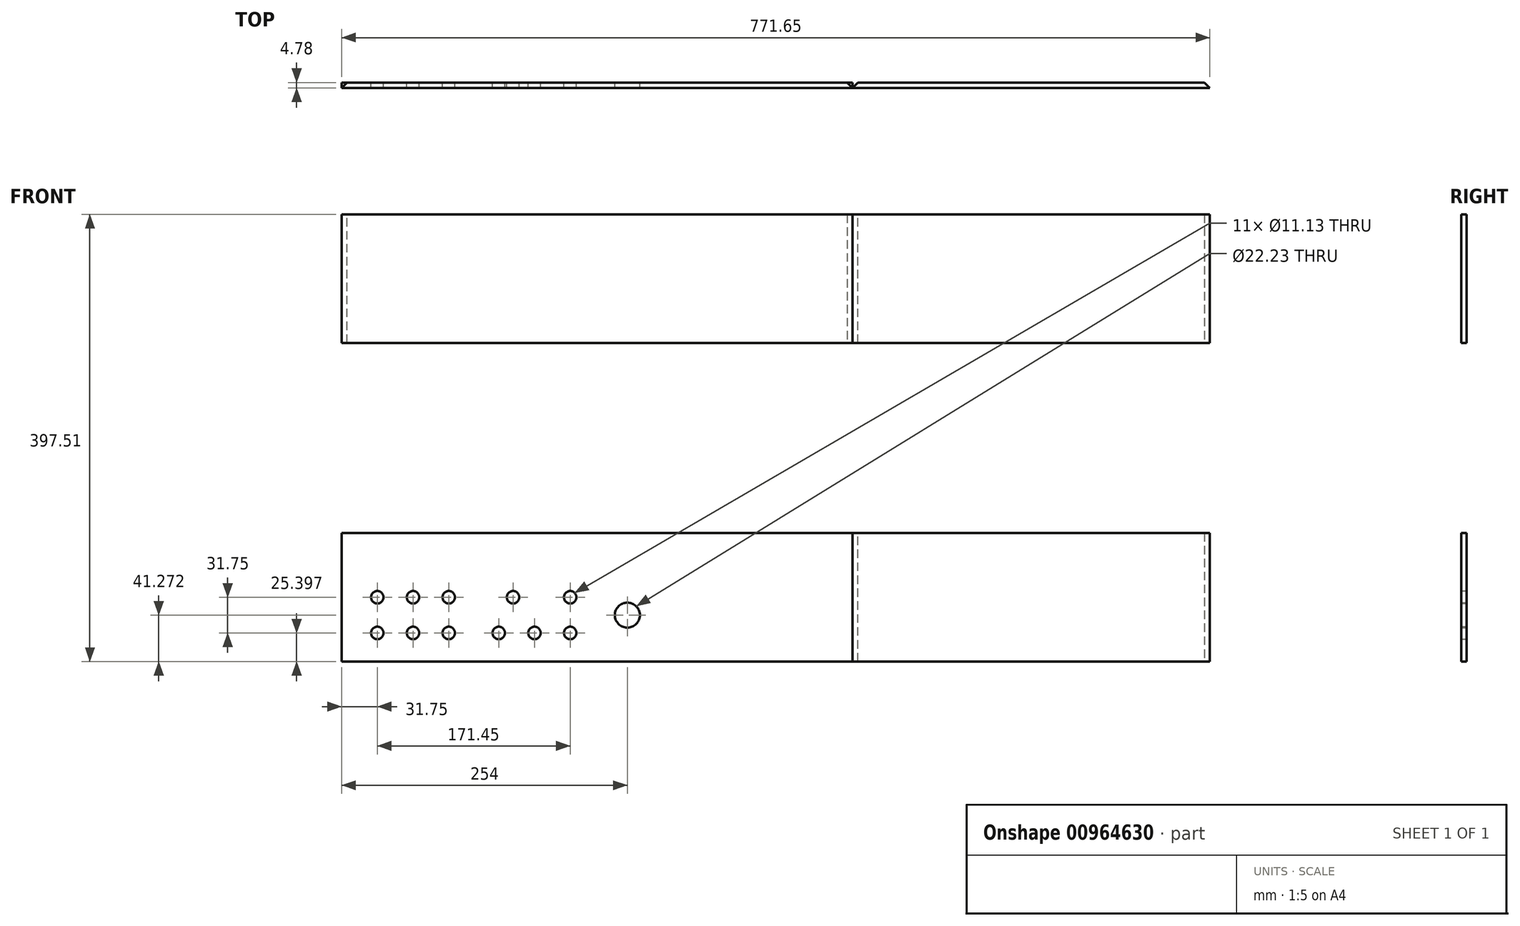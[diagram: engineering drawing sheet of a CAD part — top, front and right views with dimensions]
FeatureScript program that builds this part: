
annotation { "Feature Type Name" : "Feature", "Feature Type Description" : "" }
export const myFeature = defineFeature(function(context is Context, id is Id, definition is map)
    precondition{}
    {
        {
            var Q0;
            Q0=qCreatedBy(makeId("Front.planeOp"),FACE);
            var sketch = newSketch(context, id + "F0", { "sketchPlane" : qUnion([Q0])});
            skLineSegment(sketch, "E0.bottom", {"start": v(-189.37, 59.29) * mm, "end": v(264.66, 59.29) * mm});
            skLineSegment(sketch, "E0.top", {"start": v(-189.37, -55.01) * mm, "end": v(264.66, -55.01) * mm});
            skLineSegment(sketch, "E0.left", {"start": v(-189.37, 59.29) * mm, "end": v(-189.37, -55.01) * mm});
            skLineSegment(sketch, "E0.right", {"start": v(264.66, 59.29) * mm, "end": v(264.66, -55.01) * mm});
            skCircle(sketch, "E1", {"center": v(-157.62, -29.61) * mm, "radius": 5.56 * mm});
            skCircle(sketch, "E2", {"center": v(-125.87, -29.61) * mm, "radius": 5.56 * mm});
            skCircle(sketch, "E3", {"center": v(-94.12, -29.61) * mm, "radius": 5.56 * mm});
            skCircle(sketch, "E4", {"center": v(-17.92, -29.61) * mm, "radius": 5.56 * mm});
            skCircle(sketch, "E5", {"center": v(-49.67, -29.61) * mm, "radius": 5.56 * mm});
            skCircle(sketch, "E6", {"center": v(13.83, -29.61) * mm, "radius": 5.56 * mm});
            skCircle(sketch, "E7", {"center": v(-157.62, 2.14) * mm, "radius": 5.56 * mm});
            skCircle(sketch, "E8", {"center": v(-125.87, 2.14) * mm, "radius": 5.56 * mm});
            skCircle(sketch, "E9", {"center": v(-94.12, 2.14) * mm, "radius": 5.56 * mm});
            skCircle(sketch, "E10", {"center": v(-36.97, 2.14) * mm, "radius": 5.56 * mm});
            skCircle(sketch, "E11", {"center": v(13.83, 2.14) * mm, "radius": 5.56 * mm});
            skPoint(sketch, "E12", {"position": v(-157.62, -3.51) * mm});
            skCircle(sketch, "E13", {"center": v(64.63, -13.74) * mm, "radius": 11.11 * mm});
            skLineSegment(sketch, "E14", {"start": v(30.11, 2.14) * mm, "end": v(-174.63, 2.14) * mm, "construction": true});
            skLineSegment(sketch, "E15", {"start": v(-175, -29.61) * mm, "end": v(32.3, -29.61) * mm, "construction": true});
            skLineSegment(sketch, "E16", {"start": v(35.92, -13.74) * mm, "end": v(93.64, -13.74) * mm, "construction": true});
            skLineSegment(sketch, "E17.bottom", {"start": v(-189.37, 342.5) * mm, "end": v(264.66, 342.5) * mm});
            skLineSegment(sketch, "E17.top", {"start": v(-189.37, 228.2) * mm, "end": v(264.66, 228.2) * mm});
            skLineSegment(sketch, "E17.left", {"start": v(-189.37, 342.5) * mm, "end": v(-189.37, 228.2) * mm});
            skLineSegment(sketch, "E17.right", {"start": v(264.66, 342.5) * mm, "end": v(264.66, 228.2) * mm});
            skLineSegment(sketch, "E18.bottom", {"start": v(264.78, 59.29) * mm, "end": v(582.28, 59.29) * mm});
            skLineSegment(sketch, "E18.top", {"start": v(264.78, -55.01) * mm, "end": v(582.28, -55.01) * mm});
            skLineSegment(sketch, "E18.left", {"start": v(264.78, 59.29) * mm, "end": v(264.78, -55.01) * mm});
            skLineSegment(sketch, "E18.right", {"start": v(582.28, 59.29) * mm, "end": v(582.28, -55.01) * mm});
            skLineSegment(sketch, "E19.bottom", {"start": v(264.71, 342.5) * mm, "end": v(582.21, 342.5) * mm});
            skLineSegment(sketch, "E19.top", {"start": v(264.71, 228.2) * mm, "end": v(582.21, 228.2) * mm});
            skLineSegment(sketch, "E19.left", {"start": v(264.71, 342.5) * mm, "end": v(264.71, 228.2) * mm});
            skLineSegment(sketch, "E19.right", {"start": v(582.21, 342.5) * mm, "end": v(582.21, 228.2) * mm});
            skPoint(sketch, "E20", {"position": v(-189.37, 2.14) * mm});
            skSolve(sketch);
        }
        {
            var Q0;
            Q0=makeQuery(id+"F0.imprint","IMPRINT",FACE,{"disambiguationData":[TD([[makeQuery(id+"F0.imprint","IMPRINT",EDGE,{"derivedFrom":sQuery(id+"F0.wireOp",EDGE,"545v1GDX-f99N-rFf9-VLLV-KYLq5Sl5wzxr.bottom")}),1.0]])]});
            var Q1;
            Q1=makeQuery(id+"F0.imprint","IMPRINT",FACE,{"disambiguationData":[TD([[makeQuery(id+"F0.imprint","IMPRINT",EDGE,{"derivedFrom":sQuery(id+"F0.wireOp",EDGE,"E0.bottom")}),-1.0]])]});
            var Q2;
            Q2=makeQuery(id+"F0.imprint","IMPRINT",FACE,{"disambiguationData":[TD([[makeQuery(id+"F0.imprint","IMPRINT",EDGE,{"derivedFrom":sQuery(id+"F0.wireOp",EDGE,"mhuvXMkW-k5QU-e71L-HkeC-ZcxIXtxDrWED.bottom")}),-1.0]])]});
            var Q3;
            Q3=makeQuery(id+"F0.imprint","IMPRINT",FACE,{"disambiguationData":[TD([[makeQuery(id+"F0.imprint","IMPRINT",EDGE,{"derivedFrom":sQuery(id+"F0.wireOp",EDGE,"E17.bottom")}),-1.0]])]});
            var Q4;
            Q4=makeQuery(id+"F0.imprint","IMPRINT",FACE,{"disambiguationData":[TD([[makeQuery(id+"F0.imprint","IMPRINT",EDGE,{"derivedFrom":sQuery(id+"F0.wireOp",EDGE,"c9704ad7-6529-4927-9bfb-224757631aca.bottom")}),-1.0]])]});
            var Q5;
            Q5=makeQuery(id+"F0.imprint","IMPRINT",FACE,{"disambiguationData":[TD([[makeQuery(id+"F0.imprint","IMPRINT",EDGE,{"derivedFrom":sQuery(id+"F0.wireOp",EDGE,"E18.bottom")}),-1.0]])]});
            var Q6;
            Q6=makeQuery(id+"F0.imprint","IMPRINT",FACE,{"disambiguationData":[TD([[makeQuery(id+"F0.imprint","IMPRINT",EDGE,{"derivedFrom":sQuery(id+"F0.wireOp",EDGE,"E19.bottom")}),-1.0]])]});
            extrude(context, id + "F1", {"entities" : qUnion([Q0, Q1, Q2, Q3, Q4, Q5, Q6]), "depth" : 4.78 * mm, "offsetDistance" : 25.4 * mm});
        }
        {
            var Q0;
            Q0=makeQuery(id+"F1.opExtrude","CAP_EDGE",EDGE,{"disambiguationData":[OSD([sQuery(id+"F0.wireOp",EDGE,"E17.right")])],"isStart":true});
            var Q1;
            Q1=makeQuery(id+"F1.opExtrude","CAP_EDGE",EDGE,{"disambiguationData":[OSD([sQuery(id+"F0.wireOp",EDGE,"nuOChE4Q-GeEQ-fmZ5-sQOg-7unvAZLmPYGS.right")])],"isStart":true});
            var Q2;
            Q2=makeQuery(id+"F1.opExtrude","CAP_EDGE",EDGE,{"disambiguationData":[OSD([sQuery(id+"F0.wireOp",EDGE,"nuOChE4Q-GeEQ-fmZ5-sQOg-7unvAZLmPYGS.left")])],"isStart":true});
            var Q3;
            Q3=makeQuery(id+"F1.opExtrude","CAP_EDGE",EDGE,{"disambiguationData":[OSD([sQuery(id+"F0.wireOp",EDGE,"B0YEpUnT-bHue-zKPS-oTuu-Fwo21ukIs0fQ.right")])],"isStart":true});
            var Q4;
            Q4=makeQuery(id+"F1.opExtrude","CAP_EDGE",EDGE,{"disambiguationData":[OSD([sQuery(id+"F0.wireOp",EDGE,"E0.right")])],"isStart":true});
            var Q5;
            Q5=makeQuery(id+"F1.opExtrude","CAP_EDGE",EDGE,{"disambiguationData":[OSD([sQuery(id+"F0.wireOp",EDGE,"E0.left")])],"isStart":true});
            var Q6;
            Q6=makeQuery(id+"F1.opExtrude","CAP_EDGE",EDGE,{"disambiguationData":[OSD([sQuery(id+"F0.wireOp",EDGE,"6243fc9e-a803-4f9e-ac64-01b7eac565c9.left")])],"isStart":true});
            var Q7;
            Q7=makeQuery(id+"F1.opExtrude","CAP_EDGE",EDGE,{"disambiguationData":[OSD([sQuery(id+"F0.wireOp",EDGE,"545v1GDX-f99N-rFf9-VLLV-KYLq5Sl5wzxr.right")])],"isStart":true});
            var Q8;
            Q8=makeQuery(id+"F1.opExtrude","CAP_EDGE",EDGE,{"disambiguationData":[OSD([sQuery(id+"F0.wireOp",EDGE,"E17.left")])],"isStart":true});
            var Q9;
            Q9=makeQuery(id+"F1.opExtrude","CAP_EDGE",EDGE,{"disambiguationData":[OSD([sQuery(id+"F0.wireOp",EDGE,"mhuvXMkW-k5QU-e71L-HkeC-ZcxIXtxDrWED.right")])],"isStart":true});
            var Q10;
            Q10=makeQuery(id+"F1.opExtrude","CAP_EDGE",EDGE,{"disambiguationData":[OSD([sQuery(id+"F0.wireOp",EDGE,"a2b257b9-3a88-4484-a7b0-7f61f39d5811.right")])],"isStart":true});
            var Q11;
            Q11=makeQuery(id+"F1.opExtrude","CAP_EDGE",EDGE,{"disambiguationData":[OSD([sQuery(id+"F0.wireOp",EDGE,"c9704ad7-6529-4927-9bfb-224757631aca.right")])],"isStart":true});
            var Q12;
            Q12=makeQuery(id+"F1.opExtrude","CAP_EDGE",EDGE,{"disambiguationData":[OSD([sQuery(id+"F0.wireOp",EDGE,"E18.right")])],"isStart":true});
            var Q13;
            Q13=makeQuery(id+"F1.opExtrude","CAP_EDGE",EDGE,{"disambiguationData":[OSD([sQuery(id+"F0.wireOp",EDGE,"E18.left")])],"isStart":true});
            var Q14;
            Q14=makeQuery(id+"F1.opExtrude","CAP_EDGE",EDGE,{"disambiguationData":[OSD([sQuery(id+"F0.wireOp",EDGE,"E19.left")])],"isStart":true});
            var Q15;
            Q15=makeQuery(id+"F1.opExtrude","CAP_EDGE",EDGE,{"disambiguationData":[OSD([sQuery(id+"F0.wireOp",EDGE,"E19.right")])],"isStart":true});
            chamfer(context, id + "F2", {"entities" : qUnion([Q0, Q1, Q2, Q3, Q4, Q5, Q6, Q7, Q8, Q9, Q10, Q11, Q12, Q13, Q14, Q15]), "width" : 4.78 * mm, "tangentPropagation" : true});
        }
    });
